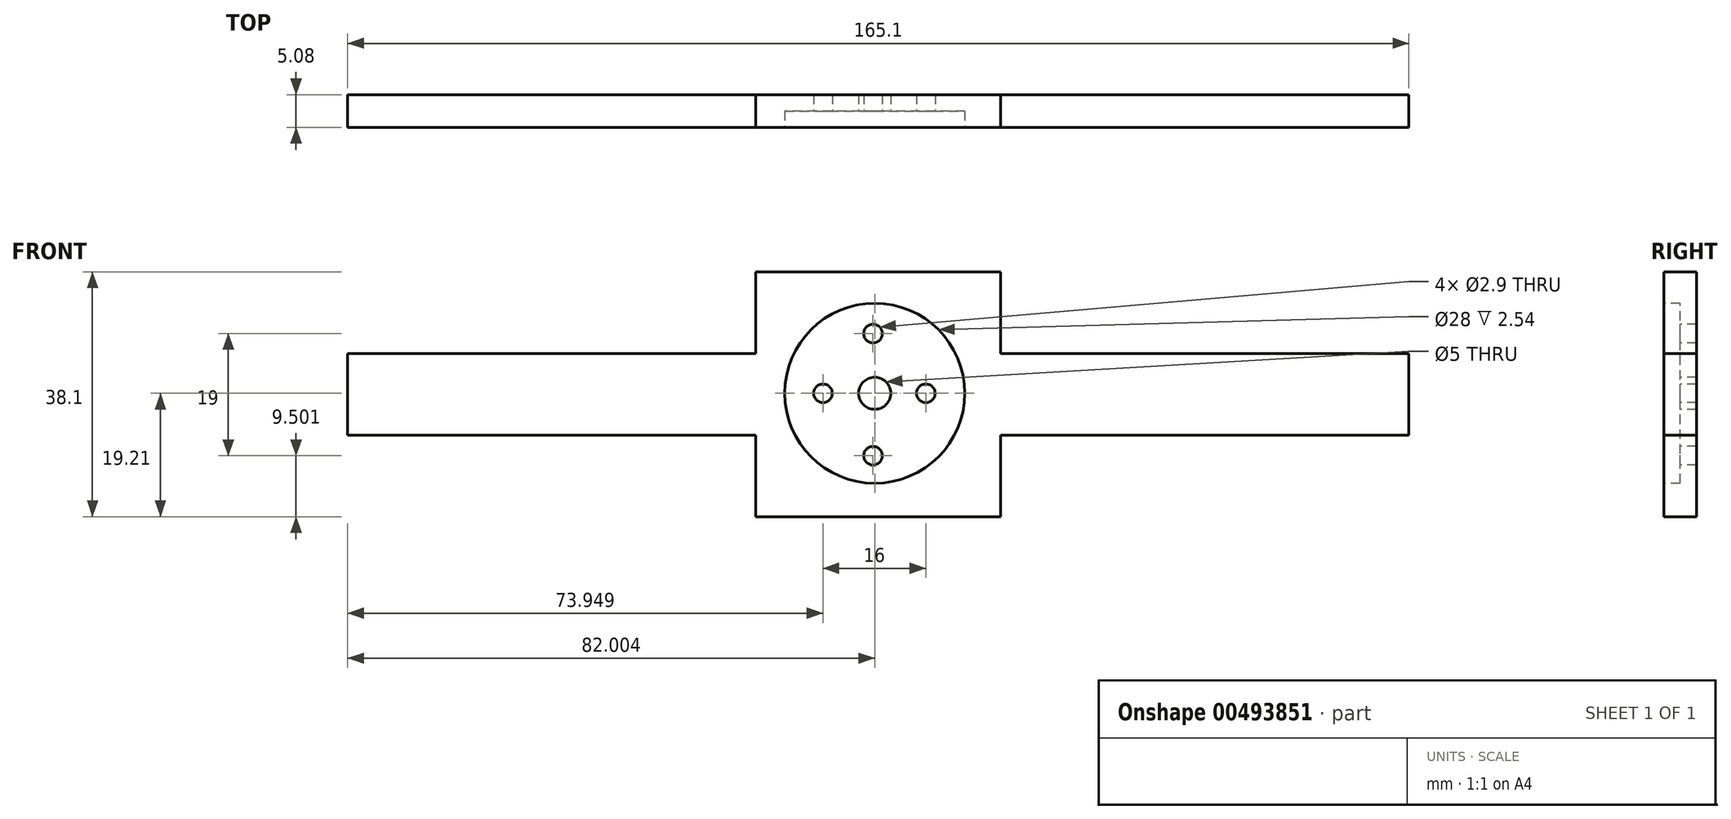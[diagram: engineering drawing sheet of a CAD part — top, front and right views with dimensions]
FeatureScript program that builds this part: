
annotation { "Feature Type Name" : "Feature", "Feature Type Description" : "" }
export const myFeature = defineFeature(function(context is Context, id is Id, definition is map)
    precondition{}
    {
        {
            var Q0;
            Q0=qCreatedBy(makeId("Front.planeOp"),FACE);
            var sketch = newSketch(context, id + "F0", { "sketchPlane" : qUnion([Q0])});
            skLineSegment(sketch, "E0.bottom", {"start": v(-50.67, 2.7) * mm, "end": v(114.43, 2.7) * mm});
            skLineSegment(sketch, "E0.top", {"start": v(-50.67, -10) * mm, "end": v(114.43, -10) * mm});
            skLineSegment(sketch, "E0.left", {"start": v(-50.67, 2.7) * mm, "end": v(-50.67, -10) * mm});
            skLineSegment(sketch, "E0.right", {"start": v(114.43, 2.7) * mm, "end": v(114.43, -10) * mm});
            skLineSegment(sketch, "E1.bottom", {"start": v(12.83, 15.4) * mm, "end": v(50.93, 15.4) * mm});
            skLineSegment(sketch, "E1.top", {"start": v(12.83, -22.7) * mm, "end": v(50.93, -22.7) * mm});
            skLineSegment(sketch, "E1.left", {"start": v(12.83, 15.4) * mm, "end": v(12.83, -22.7) * mm});
            skLineSegment(sketch, "E1.right", {"start": v(50.93, 15.4) * mm, "end": v(50.93, -22.7) * mm});
            skSolve(sketch);
        }
        {
            var Q0;
            Q0 = qSketchRegion(id + "F0", true);
            extrude(context, id + "F1", {"entities" : qUnion([Q0]), "depth" : 5.08 * mm, "offsetDistance" : 25.4 * mm});
        }
        {
            var Q0;
            Q0=makeQuery(id+"F1.opExtrude","CAP_FACE",FACE,{"disambiguationData":[OSD([sQuery(id+"F0.wireOp",EDGE,"E0.bottom"),sQuery(id+"F0.wireOp",EDGE,"E0.top"),sQuery(id+"F0.wireOp",EDGE,"E0.left"),sQuery(id+"F0.wireOp",EDGE,"E0.right"),sQuery(id+"F0.wireOp",EDGE,"E1.bottom"),sQuery(id+"F0.wireOp",EDGE,"E1.top"),sQuery(id+"F0.wireOp",EDGE,"E1.left"),sQuery(id+"F0.wireOp",EDGE,"E1.right")])],"isStart":false});
            var sketch = newSketch(context, id + "F2", { "sketchPlane" : qUnion([Q0])});
            skCircle(sketch, "E2", {"center": v(31.33, -3.5) * mm, "radius": 14 * mm});
            skSolve(sketch);
        }
        {
            var Q0;
            Q0 = qSketchRegion(id + "F2", true);
            extrude(context, id + "F3", {"entities" : qUnion([Q0]), "operationType" : NewBodyOperationType.REMOVE, "oppositeDirection" : true, "depth" : 2.54 * mm, "offsetDistance" : 25.4 * mm});
        }
        {
            var Q0;
            Q0=makeQuery(id+"F3.boolean.opBoolean","COPY",FACE,{"derivedFrom":makeQuery(id+"F3.opExtrude","CAP_FACE",FACE,{"disambiguationData":[OSD([sQuery(id+"F2.wireOp",EDGE,"E2")])],"isStart":false})});
            var sketch = newSketch(context, id + "F4", { "sketchPlane" : qUnion([Q0])});
            skCircle(sketch, "E3", {"center": v(39.28, -3.5) * mm, "radius": 1.45 * mm});
            skCircle(sketch, "E4", {"center": v(23.28, -3.5) * mm, "radius": 1.45 * mm});
            skCircle(sketch, "E5", {"center": v(31.07, -13.2) * mm, "radius": 1.45 * mm});
            skCircle(sketch, "E6", {"center": v(31.07, 5.8) * mm, "radius": 1.45 * mm});
            skCircle(sketch, "E7", {"center": v(31.33, -3.5) * mm, "radius": 2.5 * mm});
            skSolve(sketch);
        }
        {
            var Q0;
            Q0 = qSketchRegion(id + "F4", true);
            extrude(context, id + "F5", {"entities" : qUnion([Q0]), "operationType" : NewBodyOperationType.REMOVE, "oppositeDirection" : true, "depth" : 25.4 * mm, "offsetDistance" : 25.4 * mm});
        }
    });
